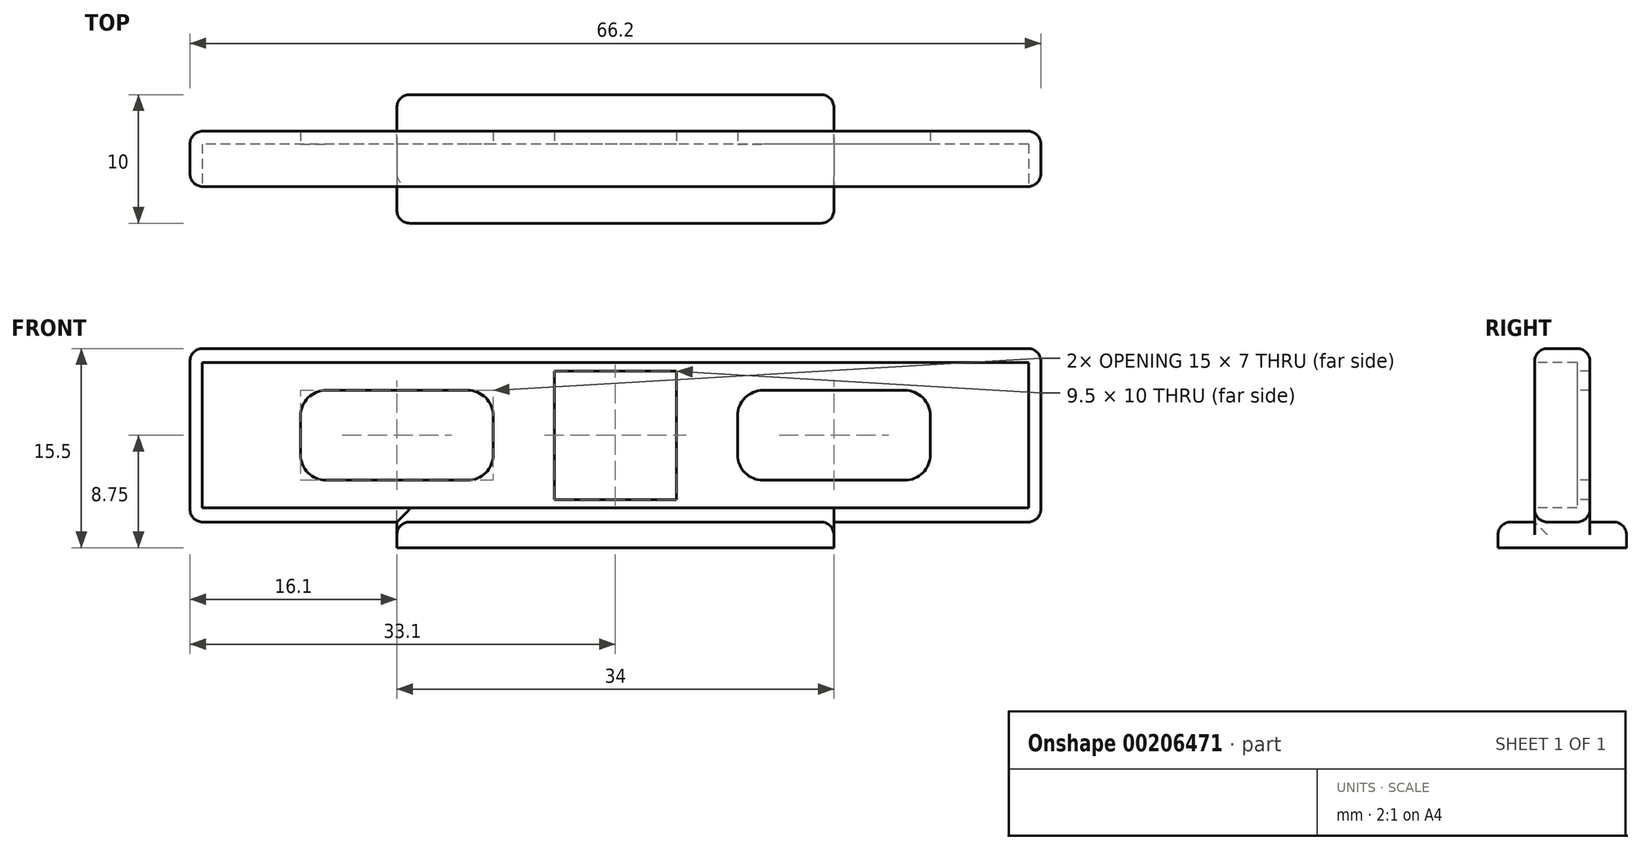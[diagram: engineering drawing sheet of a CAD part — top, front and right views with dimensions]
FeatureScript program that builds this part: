
annotation { "Feature Type Name" : "Feature", "Feature Type Description" : "" }
export const myFeature = defineFeature(function(context is Context, id is Id, definition is map)
    precondition{}
    {
        {
            var Q0;
            Q0=qCreatedBy(makeId("Top.planeOp"),FACE);
            var sketch = newSketch(context, id + "F0", { "sketchPlane" : qUnion([Q0])});
            skLineSegment(sketch, "E0.bottom", {"start": v(17, 5) * mm, "end": v(-17, 5) * mm});
            skLineSegment(sketch, "E0.top", {"start": v(17, -5) * mm, "end": v(-17, -5) * mm});
            skLineSegment(sketch, "E0.left", {"start": v(17, 5) * mm, "end": v(17, -5) * mm});
            skLineSegment(sketch, "E0.right", {"start": v(-17, 5) * mm, "end": v(-17, -5) * mm});
            skPoint(sketch, "E0.middle", {"position": v(0, 0) * mm});
            skSolve(sketch);
        }
        {
            var Q0;
            Q0 = qSketchRegion(id + "F0", true);
            extrude(context, id + "F1", {"entities" : qUnion([Q0]), "depth" : 2 * mm});
        }
        {
            var Q0;
            Q0=makeQuery(id+"F1.opExtrude","CAP_FACE",FACE,{"disambiguationData":[OSD([sQuery(id+"F0.wireOp",EDGE,"E0.bottom"),sQuery(id+"F0.wireOp",EDGE,"E0.top"),sQuery(id+"F0.wireOp",EDGE,"E0.left"),sQuery(id+"F0.wireOp",EDGE,"E0.right")])],"isStart":false});
            var sketch = newSketch(context, id + "F2", { "sketchPlane" : qUnion([Q0])});
            skLineSegment(sketch, "E1.bottom", {"start": v(33.1, 2.15) * mm, "end": v(-33.1, 2.15) * mm});
            skLineSegment(sketch, "E1.top", {"start": v(33.1, -2.15) * mm, "end": v(-33.1, -2.15) * mm});
            skLineSegment(sketch, "E1.left", {"start": v(33.1, 2.15) * mm, "end": v(33.1, -2.15) * mm});
            skLineSegment(sketch, "E1.right", {"start": v(-33.1, 2.15) * mm, "end": v(-33.1, -2.15) * mm});
            skPoint(sketch, "E1.middle", {"position": v(0, 0) * mm});
            skSolve(sketch);
        }
        {
            var Q0;
            Q0 = qSketchRegion(id + "F2", true);
            extrude(context, id + "F3", {"entities" : qUnion([Q0]), "operationType" : NewBodyOperationType.ADD, "depth" : 13.5 * mm});
        }
        {
            var Q0;
            Q0=makeQuery(id+"F3.opExtrude","SWEPT_FACE",FACE,{"disambiguationData":[OSD([sQuery(id+"F2.wireOp",EDGE,"E1.top")])]});
            var sketch = newSketch(context, id + "F4", { "sketchPlane" : qUnion([Q0])});
            skLineSegment(sketch, "E2.bottom", {"start": v(32.15, 14.4) * mm, "end": v(-32.15, 14.4) * mm});
            skLineSegment(sketch, "E2.top", {"start": v(32.15, 3.1) * mm, "end": v(-32.15, 3.1) * mm});
            skLineSegment(sketch, "E2.left", {"start": v(32.15, 14.4) * mm, "end": v(32.15, 3.1) * mm});
            skLineSegment(sketch, "E2.right", {"start": v(-32.15, 14.4) * mm, "end": v(-32.15, 3.1) * mm});
            skPoint(sketch, "E2.middle", {"position": v(0, 8.75) * mm});
            skPoint(sketch, "E2.middle.positionSnap0", {"position": v(-33.1, 8.75) * mm});
            skPoint(sketch, "E2.middle.positionSnap1", {"position": v(0, 2) * mm});
            skPoint(sketch, "E2.centerSnap0", {"position": v(-33.1, 8.75) * mm});
            skPoint(sketch, "E2.centerSnap1", {"position": v(0, 2) * mm});
            skLineSegment(sketch, "E3.bottom", {"start": v(4.75, 13.75) * mm, "end": v(-4.75, 13.75) * mm});
            skLineSegment(sketch, "E3.top", {"start": v(4.75, 3.75) * mm, "end": v(-4.75, 3.75) * mm});
            skLineSegment(sketch, "E3.left", {"start": v(4.75, 13.75) * mm, "end": v(4.75, 3.75) * mm});
            skLineSegment(sketch, "E3.right", {"start": v(-4.75, 13.75) * mm, "end": v(-4.75, 3.75) * mm});
            skLineSegment(sketch, "E4.bottom", {"start": v(-11.5, 12.25) * mm, "end": v(-22.5, 12.25) * mm});
            skLineSegment(sketch, "E4.top", {"start": v(-11.5, 5.25) * mm, "end": v(-22.5, 5.25) * mm});
            skLineSegment(sketch, "E4.left", {"start": v(-9.5, 10.25) * mm, "end": v(-9.5, 7.25) * mm});
            skLineSegment(sketch, "E4.right", {"start": v(-24.5, 10.25) * mm, "end": v(-24.5, 7.25) * mm});
            skPoint(sketch, "E4.middle", {"position": v(-17, 8.75) * mm});
            skLineSegment(sketch, "E5.bottom", {"start": v(22.5, 12.25) * mm, "end": v(11.5, 12.25) * mm});
            skLineSegment(sketch, "E5.top", {"start": v(22.5, 5.25) * mm, "end": v(11.5, 5.25) * mm});
            skLineSegment(sketch, "E5.left", {"start": v(24.5, 10.25) * mm, "end": v(24.5, 7.25) * mm});
            skLineSegment(sketch, "E5.right", {"start": v(9.5, 10.25) * mm, "end": v(9.5, 7.25) * mm});
            skPoint(sketch, "E5.middle", {"position": v(17, 8.75) * mm});
            skPoint(sketch, "E6.visualSharp", {"position": v(-24.5, 12.25) * mm});
            skArc(sketch, "E6.filletArc", {"start": v(-22.5, 12.25) * mm, "mid": v(-23.91, 11.66) * mm, "end": v(-24.5, 10.25) * mm});
            skPoint(sketch, "E7.visualSharp", {"position": v(-24.5, 5.25) * mm});
            skArc(sketch, "E7.filletArc", {"start": v(-24.5, 7.25) * mm, "mid": v(-23.91, 5.84) * mm, "end": v(-22.5, 5.25) * mm});
            skPoint(sketch, "E8.visualSharp", {"position": v(-9.5, 5.25) * mm});
            skArc(sketch, "E8.filletArc", {"start": v(-11.5, 5.25) * mm, "mid": v(-10.09, 5.84) * mm, "end": v(-9.5, 7.25) * mm});
            skPoint(sketch, "E9.visualSharp", {"position": v(-9.5, 12.25) * mm});
            skArc(sketch, "E9.filletArc", {"start": v(-9.5, 10.25) * mm, "mid": v(-10.09, 11.66) * mm, "end": v(-11.5, 12.25) * mm});
            skPoint(sketch, "E10.visualSharp", {"position": v(9.5, 12.25) * mm});
            skArc(sketch, "E10.filletArc", {"start": v(11.5, 12.25) * mm, "mid": v(10.09, 11.66) * mm, "end": v(9.5, 10.25) * mm});
            skPoint(sketch, "E11.visualSharp", {"position": v(24.5, 12.25) * mm});
            skArc(sketch, "E11.filletArc", {"start": v(24.5, 10.25) * mm, "mid": v(23.91, 11.66) * mm, "end": v(22.5, 12.25) * mm});
            skPoint(sketch, "E12.visualSharp", {"position": v(24.5, 5.25) * mm});
            skArc(sketch, "E12.filletArc", {"start": v(22.5, 5.25) * mm, "mid": v(23.91, 5.84) * mm, "end": v(24.5, 7.25) * mm});
            skPoint(sketch, "E13.visualSharp", {"position": v(9.5, 5.25) * mm});
            skArc(sketch, "E13.filletArc", {"start": v(9.5, 7.25) * mm, "mid": v(10.09, 5.84) * mm, "end": v(11.5, 5.25) * mm});
            skSolve(sketch);
        }
        {
            var Q0;
            Q0=makeQuery(id+"F4.imprint","IMPRINT",FACE,{"disambiguationData":[TD([[makeQuery(id+"F4.imprint","IMPRINT",EDGE,{"derivedFrom":sQuery(id+"F4.wireOp",EDGE,"E2.bottom")}),1.0]])]});
            extrude(context, id + "F5", {"entities" : qUnion([Q0]), "operationType" : NewBodyOperationType.REMOVE, "oppositeDirection" : true, "depth" : 3.3 * mm});
        }
        {
            var Q0;
            Q0=makeQuery(id+"F4.imprint","IMPRINT",FACE,{"disambiguationData":[TD([[makeQuery(id+"F4.imprint","IMPRINT",EDGE,{"derivedFrom":sQuery(id+"F4.wireOp",EDGE,"E5.bottom")}),1.0]])]});
            var Q1;
            Q1=makeQuery(id+"F4.imprint","IMPRINT",FACE,{"disambiguationData":[TD([[makeQuery(id+"F4.imprint","IMPRINT",EDGE,{"derivedFrom":sQuery(id+"F4.wireOp",EDGE,"E3.bottom")}),1.0]])]});
            var Q2;
            Q2=makeQuery(id+"F4.imprint","IMPRINT",FACE,{"disambiguationData":[TD([[makeQuery(id+"F4.imprint","IMPRINT",EDGE,{"derivedFrom":sQuery(id+"F4.wireOp",EDGE,"E4.bottom")}),1.0]])]});
            extrude(context, id + "F6", {"entities" : qUnion([Q0, Q1, Q2]), "operationType" : NewBodyOperationType.REMOVE, "oppositeDirection" : true, "depth" : 25 * mm, "hasSecondDirection" : true, "secondDirectionOppositeDirection" : false, "secondDirectionDepth" : 25 * mm});
        }
        {
            var Q0;
            {var subQ0=sQuery(id+"F2.wireOp",EDGE,"E1.top");var subQ1=makeQuery(id+"F3.opExtrude","SWEPT_FACE",FACE,{"disambiguationData":[OSD([subQ0])]});var subQ2=sQuery(id+"F0.wireOp",EDGE,"E0.left");var subQ3=sQuery(id+"F2.wireOp",EDGE,"E1.left");var subQ4=makeQuery(id+"F3.opExtrude","CAP_FACE",FACE,{"disambiguationData":[OSD([sQuery(id+"F2.wireOp",EDGE,"E1.bottom"),subQ0,subQ3,sQuery(id+"F2.wireOp",EDGE,"E1.right")])],"isStart":true});Q0=makeQuery(id+"F3.boolean.opBoolean","SPLIT",EDGE,{"disambiguationData":[topologyDisambiguationEdgeConnected([subQ4,subQ1]),TD([makeQuery(id+"F1.opExtrude","SWEPT_FACE",FACE,{"disambiguationData":[OSD([subQ2])]})])],"derivedFrom":makeQuery(id+"F3.opExtrude","CAP_EDGE",EDGE,{"disambiguationData":[OSD([subQ0])],"isStart":true})});}
            var Q1;
            {var subQ0=sQuery(id+"F2.wireOp",EDGE,"E1.top");var subQ1=makeQuery(id+"F3.opExtrude","SWEPT_FACE",FACE,{"disambiguationData":[OSD([subQ0])]});var subQ2=sQuery(id+"F2.wireOp",EDGE,"E1.right");var subQ3=makeQuery(id+"F3.opExtrude","CAP_FACE",FACE,{"disambiguationData":[OSD([sQuery(id+"F2.wireOp",EDGE,"E1.bottom"),subQ0,sQuery(id+"F2.wireOp",EDGE,"E1.left"),subQ2])],"isStart":true});var subQ4=sQuery(id+"F0.wireOp",EDGE,"E0.right");Q1=makeQuery(id+"F3.boolean.opBoolean","SPLIT",EDGE,{"disambiguationData":[topologyDisambiguationEdgeConnected([subQ3,subQ1]),TD([makeQuery(id+"F1.opExtrude","SWEPT_FACE",FACE,{"disambiguationData":[OSD([subQ4])]})])],"derivedFrom":makeQuery(id+"F3.opExtrude","CAP_EDGE",EDGE,{"disambiguationData":[OSD([subQ0])],"isStart":true})});}
            var Q2;
            Q2=makeQuery(id+"F3.opExtrude","SWEPT_EDGE",EDGE,{"disambiguationData":[OSD([sQuery(id+"F2.wireOp",EDGE,"E1.top"),sQuery(id+"F2.wireOp",EDGE,"E1.left")])]});
            var Q3;
            Q3=makeQuery(id+"F3.opExtrude","CAP_EDGE",EDGE,{"disambiguationData":[OSD([sQuery(id+"F2.wireOp",EDGE,"E1.right")])],"isStart":true});
            var Q4;
            Q4=makeQuery(id+"F3.opExtrude","SWEPT_EDGE",EDGE,{"disambiguationData":[OSD([sQuery(id+"F2.wireOp",EDGE,"E1.top"),sQuery(id+"F2.wireOp",EDGE,"E1.right")])]});
            var Q5;
            Q5=makeQuery(id+"F3.opExtrude","SWEPT_EDGE",EDGE,{"disambiguationData":[OSD([sQuery(id+"F2.wireOp",EDGE,"E1.bottom"),sQuery(id+"F2.wireOp",EDGE,"E1.right")])]});
            var Q6;
            {var subQ0=sQuery(id+"F2.wireOp",EDGE,"E1.right");var subQ1=sQuery(id+"F2.wireOp",EDGE,"E1.bottom");var subQ2=makeQuery(id+"F3.opExtrude","CAP_FACE",FACE,{"disambiguationData":[OSD([subQ1,sQuery(id+"F2.wireOp",EDGE,"E1.top"),sQuery(id+"F2.wireOp",EDGE,"E1.left"),subQ0])],"isStart":true});var subQ3=sQuery(id+"F0.wireOp",EDGE,"E0.right");var subQ4=makeQuery(id+"F3.opExtrude","SWEPT_FACE",FACE,{"disambiguationData":[OSD([subQ1])]});Q6=makeQuery(id+"F3.boolean.opBoolean","SPLIT",EDGE,{"disambiguationData":[topologyDisambiguationEdgeConnected([subQ4,subQ2]),TD([makeQuery(id+"F1.opExtrude","SWEPT_FACE",FACE,{"disambiguationData":[OSD([subQ3])]})])],"derivedFrom":makeQuery(id+"F3.opExtrude","CAP_EDGE",EDGE,{"disambiguationData":[OSD([subQ1])],"isStart":true})});}
            var Q7;
            Q7=makeQuery(id+"F3.opExtrude","CAP_EDGE",EDGE,{"disambiguationData":[OSD([sQuery(id+"F2.wireOp",EDGE,"E1.right")])],"isStart":false});
            var Q8;
            Q8=makeQuery(id+"F3.opExtrude","CAP_EDGE",EDGE,{"disambiguationData":[OSD([sQuery(id+"F2.wireOp",EDGE,"E1.bottom")])],"isStart":false});
            var Q9;
            Q9=makeQuery(id+"F3.opExtrude","CAP_EDGE",EDGE,{"disambiguationData":[OSD([sQuery(id+"F2.wireOp",EDGE,"E1.top")])],"isStart":false});
            var Q10;
            Q10=makeQuery(id+"F3.opExtrude","CAP_EDGE",EDGE,{"disambiguationData":[OSD([sQuery(id+"F2.wireOp",EDGE,"E1.left")])],"isStart":false});
            var Q11;
            Q11=makeQuery(id+"F3.opExtrude","CAP_EDGE",EDGE,{"disambiguationData":[OSD([sQuery(id+"F2.wireOp",EDGE,"E1.left")])],"isStart":true});
            var Q12;
            Q12=makeQuery(id+"F3.opExtrude","SWEPT_EDGE",EDGE,{"disambiguationData":[OSD([sQuery(id+"F2.wireOp",EDGE,"E1.bottom"),sQuery(id+"F2.wireOp",EDGE,"E1.left")])]});
            var Q13;
            {var subQ0=sQuery(id+"F2.wireOp",EDGE,"E1.bottom");var subQ1=makeQuery(id+"F3.opExtrude","SWEPT_FACE",FACE,{"disambiguationData":[OSD([subQ0])]});var subQ2=sQuery(id+"F2.wireOp",EDGE,"E1.left");var subQ3=makeQuery(id+"F3.opExtrude","CAP_FACE",FACE,{"disambiguationData":[OSD([subQ0,sQuery(id+"F2.wireOp",EDGE,"E1.top"),subQ2,sQuery(id+"F2.wireOp",EDGE,"E1.right")])],"isStart":true});var subQ4=sQuery(id+"F0.wireOp",EDGE,"E0.left");Q13=makeQuery(id+"F3.boolean.opBoolean","SPLIT",EDGE,{"disambiguationData":[topologyDisambiguationEdgeConnected([subQ1,subQ3]),TD([makeQuery(id+"F1.opExtrude","SWEPT_FACE",FACE,{"disambiguationData":[OSD([subQ4])]})])],"derivedFrom":makeQuery(id+"F3.opExtrude","CAP_EDGE",EDGE,{"disambiguationData":[OSD([subQ0])],"isStart":true})});}
            var Q14;
            Q14=makeQuery(id+"F1.opExtrude","SWEPT_EDGE",EDGE,{"disambiguationData":[OSD([sQuery(id+"F0.wireOp",EDGE,"E0.bottom"),sQuery(id+"F0.wireOp",EDGE,"E0.left")])]});
            var Q15;
            Q15=makeQuery(id+"F1.opExtrude","SWEPT_EDGE",EDGE,{"disambiguationData":[OSD([sQuery(id+"F0.wireOp",EDGE,"E0.bottom"),sQuery(id+"F0.wireOp",EDGE,"E0.right")])]});
            var Q16;
            Q16=makeQuery(id+"F1.opExtrude","CAP_EDGE",EDGE,{"disambiguationData":[OSD([sQuery(id+"F0.wireOp",EDGE,"E0.bottom")])],"isStart":false});
            var Q17;
            Q17=makeQuery(id+"F1.opExtrude","CAP_EDGE",EDGE,{"disambiguationData":[OSD([sQuery(id+"F0.wireOp",EDGE,"E0.top")])],"isStart":false});
            var Q18;
            Q18=makeQuery(id+"F1.opExtrude","SWEPT_EDGE",EDGE,{"disambiguationData":[OSD([sQuery(id+"F0.wireOp",EDGE,"E0.top"),sQuery(id+"F0.wireOp",EDGE,"E0.right")])]});
            var Q19;
            Q19=makeQuery(id+"F1.opExtrude","SWEPT_EDGE",EDGE,{"disambiguationData":[OSD([sQuery(id+"F0.wireOp",EDGE,"E0.top"),sQuery(id+"F0.wireOp",EDGE,"E0.left")])]});
            var Q20;
            Q20=makeQuery(id+"F5.boolean.opBoolean","COPY",EDGE,{"derivedFrom":makeQuery(id+"F5.opExtrude","CAP_EDGE",EDGE,{"disambiguationData":[OSD([sQuery(id+"F4.wireOp",EDGE,"E3.right")])],"isStart":false})});
            var Q21;
            Q21=makeQuery(id+"F5.boolean.opBoolean","COPY",EDGE,{"derivedFrom":makeQuery(id+"F5.opExtrude","CAP_EDGE",EDGE,{"disambiguationData":[OSD([sQuery(id+"F4.wireOp",EDGE,"E3.left")])],"isStart":false})});
            var Q22;
            Q22=makeQuery(id+"F5.boolean.opBoolean","COPY",EDGE,{"derivedFrom":makeQuery(id+"F5.opExtrude","CAP_EDGE",EDGE,{"disambiguationData":[OSD([sQuery(id+"F4.wireOp",EDGE,"E3.top")])],"isStart":false})});
            var Q23;
            Q23=makeQuery(id+"F5.boolean.opBoolean","COPY",EDGE,{"derivedFrom":makeQuery(id+"F5.opExtrude","CAP_EDGE",EDGE,{"disambiguationData":[OSD([sQuery(id+"F4.wireOp",EDGE,"E3.bottom")])],"isStart":false})});
            fillet(context, id + "F7", {"entities" : qUnion([Q0, Q1, Q2, Q3, Q4, Q5, Q6, Q7, Q8, Q9, Q10, Q11, Q12, Q13, Q14, Q15, Q16, Q17, Q18, Q19, Q20, Q21, Q22, Q23]), "radius" : 1 * mm, "tangentPropagation" : true, "allowEdgeOverflow" : false});
        }
        {
            var Q0;
            {var subQ0=sQuery(id+"F2.wireOp",EDGE,"E1.top");var subQ1=sQuery(id+"F0.wireOp",EDGE,"E0.right");Q0=makeQuery(id+"F7.opFillet","TWEAK_EDGE",EDGE,{"derivedFrom":[makeQuery(id+"F3.boolean.opBoolean","TWEAK_VERTEX",VERTEX,{"derivedFrom":[makeQuery(id+"F1.opExtrude","CAP_FACE",FACE,{"disambiguationData":[OSD([sQuery(id+"F0.wireOp",EDGE,"E0.bottom"),sQuery(id+"F0.wireOp",EDGE,"E0.top"),sQuery(id+"F0.wireOp",EDGE,"E0.left"),subQ1])],"isStart":false}),makeQuery(id+"F1.opExtrude","SWEPT_FACE",FACE,{"disambiguationData":[OSD([subQ1])]}),makeQuery(id+"F3.opExtrude","CAP_FACE",FACE,{"disambiguationData":[OSD([sQuery(id+"F2.wireOp",EDGE,"E1.bottom"),subQ0,sQuery(id+"F2.wireOp",EDGE,"E1.left"),sQuery(id+"F2.wireOp",EDGE,"E1.right")])],"isStart":true}),makeQuery(id+"F3.opExtrude","SWEPT_FACE",FACE,{"disambiguationData":[OSD([subQ0])]})]})]});}
            var Q1;
            {var subQ1=sQuery(id+"F0.wireOp",EDGE,"E0.right");var subQ2=sQuery(id+"F0.wireOp",EDGE,"E0.top");var subQ3=makeQuery(id+"F1.opExtrude","CAP_FACE",FACE,{"disambiguationData":[OSD([sQuery(id+"F0.wireOp",EDGE,"E0.bottom"),subQ2,sQuery(id+"F0.wireOp",EDGE,"E0.left"),subQ1])],"isStart":false});var subQ4=makeQuery(id+"F1.opExtrude","SWEPT_FACE",FACE,{"disambiguationData":[OSD([subQ1])]});Q1=makeQuery(id+"F3.boolean.opBoolean","SPLIT",EDGE,{"disambiguationData":[topologyDisambiguationEdgeConnected([subQ3,subQ4]),TD([makeQuery(id+"F1.opExtrude","SWEPT_FACE",FACE,{"disambiguationData":[OSD([subQ2])]})])],"derivedFrom":makeQuery(id+"F1.opExtrude","CAP_EDGE",EDGE,{"disambiguationData":[OSD([subQ1])],"isStart":false})});}
            var Q2;
            {var subQ0=sQuery(id+"F2.wireOp",EDGE,"E1.top");var subQ1=sQuery(id+"F0.wireOp",EDGE,"E0.left");Q2=makeQuery(id+"F7.opFillet","TWEAK_EDGE",EDGE,{"derivedFrom":[makeQuery(id+"F3.boolean.opBoolean","TWEAK_VERTEX",VERTEX,{"derivedFrom":[makeQuery(id+"F1.opExtrude","CAP_FACE",FACE,{"disambiguationData":[OSD([sQuery(id+"F0.wireOp",EDGE,"E0.bottom"),sQuery(id+"F0.wireOp",EDGE,"E0.top"),subQ1,sQuery(id+"F0.wireOp",EDGE,"E0.right")])],"isStart":false}),makeQuery(id+"F1.opExtrude","SWEPT_FACE",FACE,{"disambiguationData":[OSD([subQ1])]}),makeQuery(id+"F3.opExtrude","CAP_FACE",FACE,{"disambiguationData":[OSD([sQuery(id+"F2.wireOp",EDGE,"E1.bottom"),subQ0,sQuery(id+"F2.wireOp",EDGE,"E1.left"),sQuery(id+"F2.wireOp",EDGE,"E1.right")])],"isStart":true}),makeQuery(id+"F3.opExtrude","SWEPT_FACE",FACE,{"disambiguationData":[OSD([subQ0])]})]})]});}
            var Q3;
            {var subQ1=sQuery(id+"F0.wireOp",EDGE,"E0.left");var subQ2=sQuery(id+"F0.wireOp",EDGE,"E0.top");var subQ3=makeQuery(id+"F1.opExtrude","CAP_FACE",FACE,{"disambiguationData":[OSD([sQuery(id+"F0.wireOp",EDGE,"E0.bottom"),subQ2,subQ1,sQuery(id+"F0.wireOp",EDGE,"E0.right")])],"isStart":false});var subQ4=makeQuery(id+"F1.opExtrude","SWEPT_FACE",FACE,{"disambiguationData":[OSD([subQ1])]});Q3=makeQuery(id+"F3.boolean.opBoolean","SPLIT",EDGE,{"disambiguationData":[topologyDisambiguationEdgeConnected([subQ3,subQ4]),TD([makeQuery(id+"F1.opExtrude","SWEPT_FACE",FACE,{"disambiguationData":[OSD([subQ2])]})])],"derivedFrom":makeQuery(id+"F1.opExtrude","CAP_EDGE",EDGE,{"disambiguationData":[OSD([subQ1])],"isStart":false})});}
            var Q4;
            {var subQ1=sQuery(id+"F0.wireOp",EDGE,"E0.left");var subQ2=makeQuery(id+"F1.opExtrude","SWEPT_FACE",FACE,{"disambiguationData":[OSD([subQ1])]});var subQ3=sQuery(id+"F0.wireOp",EDGE,"E0.bottom");var subQ4=makeQuery(id+"F1.opExtrude","CAP_FACE",FACE,{"disambiguationData":[OSD([subQ3,sQuery(id+"F0.wireOp",EDGE,"E0.top"),subQ1,sQuery(id+"F0.wireOp",EDGE,"E0.right")])],"isStart":false});Q4=makeQuery(id+"F3.boolean.opBoolean","SPLIT",EDGE,{"disambiguationData":[topologyDisambiguationEdgeConnected([subQ4,subQ2]),TD([makeQuery(id+"F1.opExtrude","SWEPT_FACE",FACE,{"disambiguationData":[OSD([subQ3])]})])],"derivedFrom":makeQuery(id+"F1.opExtrude","CAP_EDGE",EDGE,{"disambiguationData":[OSD([subQ1])],"isStart":false})});}
            var Q5;
            {var subQ0=sQuery(id+"F2.wireOp",EDGE,"E1.bottom");var subQ1=sQuery(id+"F0.wireOp",EDGE,"E0.left");Q5=makeQuery(id+"F7.opFillet","TWEAK_EDGE",EDGE,{"derivedFrom":[makeQuery(id+"F3.boolean.opBoolean","TWEAK_VERTEX",VERTEX,{"derivedFrom":[makeQuery(id+"F1.opExtrude","CAP_FACE",FACE,{"disambiguationData":[OSD([sQuery(id+"F0.wireOp",EDGE,"E0.bottom"),sQuery(id+"F0.wireOp",EDGE,"E0.top"),subQ1,sQuery(id+"F0.wireOp",EDGE,"E0.right")])],"isStart":false}),makeQuery(id+"F1.opExtrude","SWEPT_FACE",FACE,{"disambiguationData":[OSD([subQ1])]}),makeQuery(id+"F3.opExtrude","SWEPT_FACE",FACE,{"disambiguationData":[OSD([subQ0])]}),makeQuery(id+"F3.opExtrude","CAP_FACE",FACE,{"disambiguationData":[OSD([subQ0,sQuery(id+"F2.wireOp",EDGE,"E1.top"),sQuery(id+"F2.wireOp",EDGE,"E1.left"),sQuery(id+"F2.wireOp",EDGE,"E1.right")])],"isStart":true})]})]});}
            var Q6;
            {var subQ1=sQuery(id+"F0.wireOp",EDGE,"E0.right");var subQ2=sQuery(id+"F0.wireOp",EDGE,"E0.bottom");var subQ3=makeQuery(id+"F1.opExtrude","CAP_FACE",FACE,{"disambiguationData":[OSD([subQ2,sQuery(id+"F0.wireOp",EDGE,"E0.top"),sQuery(id+"F0.wireOp",EDGE,"E0.left"),subQ1])],"isStart":false});var subQ4=makeQuery(id+"F1.opExtrude","SWEPT_FACE",FACE,{"disambiguationData":[OSD([subQ1])]});Q6=makeQuery(id+"F3.boolean.opBoolean","SPLIT",EDGE,{"disambiguationData":[topologyDisambiguationEdgeConnected([subQ3,subQ4]),TD([makeQuery(id+"F1.opExtrude","SWEPT_FACE",FACE,{"disambiguationData":[OSD([subQ2])]})])],"derivedFrom":makeQuery(id+"F1.opExtrude","CAP_EDGE",EDGE,{"disambiguationData":[OSD([subQ1])],"isStart":false})});}
            var Q7;
            {var subQ0=sQuery(id+"F2.wireOp",EDGE,"E1.bottom");var subQ1=sQuery(id+"F0.wireOp",EDGE,"E0.right");Q7=makeQuery(id+"F7.opFillet","TWEAK_EDGE",EDGE,{"derivedFrom":[makeQuery(id+"F3.boolean.opBoolean","TWEAK_VERTEX",VERTEX,{"derivedFrom":[makeQuery(id+"F1.opExtrude","CAP_FACE",FACE,{"disambiguationData":[OSD([sQuery(id+"F0.wireOp",EDGE,"E0.bottom"),sQuery(id+"F0.wireOp",EDGE,"E0.top"),sQuery(id+"F0.wireOp",EDGE,"E0.left"),subQ1])],"isStart":false}),makeQuery(id+"F1.opExtrude","SWEPT_FACE",FACE,{"disambiguationData":[OSD([subQ1])]}),makeQuery(id+"F3.opExtrude","SWEPT_FACE",FACE,{"disambiguationData":[OSD([subQ0])]}),makeQuery(id+"F3.opExtrude","CAP_FACE",FACE,{"disambiguationData":[OSD([subQ0,sQuery(id+"F2.wireOp",EDGE,"E1.top"),sQuery(id+"F2.wireOp",EDGE,"E1.left"),sQuery(id+"F2.wireOp",EDGE,"E1.right")])],"isStart":true})]})]});}
            fillet(context, id + "F8", {"entities" : qUnion([Q0, Q1, Q2, Q3, Q4, Q5, Q6, Q7]), "radius" : 1 * mm, "tangentPropagation" : true, "allowEdgeOverflow" : false});
        }
    });
